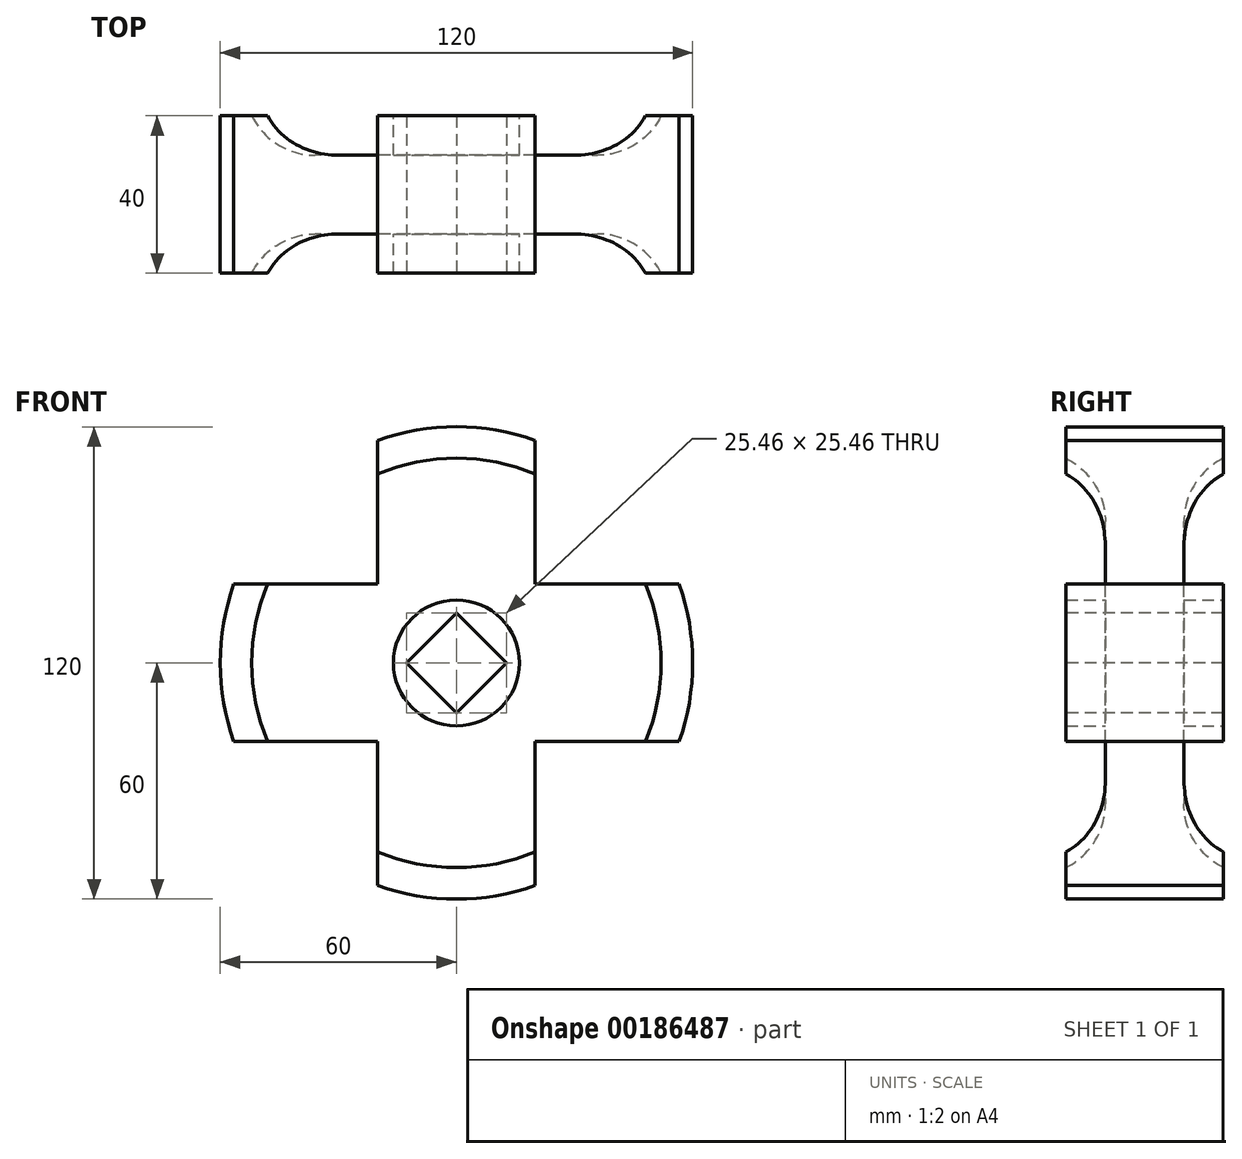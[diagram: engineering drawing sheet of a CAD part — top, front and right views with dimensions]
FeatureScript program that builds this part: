
annotation { "Feature Type Name" : "Feature", "Feature Type Description" : "" }
export const myFeature = defineFeature(function(context is Context, id is Id, definition is map)
    precondition{}
    {
        {
            var Q0;
            Q0=qCreatedBy(makeId("Top.planeOp"),FACE);
            var sketch = newSketch(context, id + "F0", { "sketchPlane" : qUnion([Q0])});
            skLineSegment(sketch, "E0", {"start": v(-60, 10) * mm, "end": v(-60, 20) * mm});
            skLineSegment(sketch, "E1", {"start": v(-60, 20) * mm, "end": v(-52, 20) * mm});
            skLineSegment(sketch, "E2", {"start": v(0, 20) * mm, "end": v(-16, 20) * mm});
            skLineSegment(sketch, "E3", {"start": v(-16, 20) * mm, "end": v(-16, 10) * mm});
            skPoint(sketch, "E4", {"position": v(-35.88, 10) * mm});
            skArc(sketch, "E5", {"start": v(-52, 20) * mm, "mid": v(-45.36, 12.7) * mm, "end": v(-35.88, 10) * mm});
            skArc(sketch, "E6.MirrorCS", {"start": v(-52, -20) * mm, "mid": v(-45.36, -12.7) * mm, "end": v(-35.88, -10) * mm});
            skLineSegment(sketch, "E7.MirrorCS", {"start": v(-60, -20) * mm, "end": v(-52, -20) * mm});
            skLineSegment(sketch, "E8.MirrorCS", {"start": v(-16, -20) * mm, "end": v(-16, -10) * mm});
            skLineSegment(sketch, "E9.MirrorCS", {"start": v(0, -20) * mm, "end": v(-16, -20) * mm});
            skLineSegment(sketch, "E10", {"start": v(-60, 10) * mm, "end": v(-60, -10) * mm});
            skLineSegment(sketch, "E11", {"start": v(-60, -10) * mm, "end": v(-60, -20) * mm});
            skLineSegment(sketch, "E12", {"start": v(0, 20) * mm, "end": v(0, -20) * mm});
            skLineSegment(sketch, "E13", {"start": v(0, 62.15) * mm, "end": v(0, -61.97) * mm, "construction": true});
            skPoint(sketch, "E14.start.orphan", {"position": v(0, 10) * mm});
            skPoint(sketch, "E15.orphan", {"position": v(-60, -10) * mm});
            skPoint(sketch, "E16.orphan", {"position": v(0, -10) * mm});
            skLineSegment(sketch, "E17", {"start": v(-16, 10) * mm, "end": v(-35.88, 10) * mm});
            skLineSegment(sketch, "E18", {"start": v(-16, -10) * mm, "end": v(-35.88, -10) * mm});
            skSolve(sketch);
        }
        {
            var Q0;
            Q0=makeQuery(id+"F0.imprint","IMPRINT",FACE,{"disambiguationData":[TD([[makeQuery(id+"F0.imprint","IMPRINT",EDGE,{"derivedFrom":sQuery(id+"F0.wireOp",EDGE,"E0")}),-1.0]])]});
            var Q1;
            Q1=sQuery(id+"F0.wireOp",EDGE,"E13");
            revolve(context, id + "F1", {"entities" : qUnion([Q0]), "axis" : qUnion([Q1]), "revolveType" : RevolveType.FULL});
        }
        {
            var Q0;
            Q0=makeQuery(id+"F1.opRevolve","SWEPT_FACE",FACE,{"disambiguationData":[OSD([sQuery(id+"F0.wireOp",EDGE,"E7.MirrorCS")])]});
            var sketch = newSketch(context, id + "F2", { "sketchPlane" : qUnion([Q0])});
            skLineSegment(sketch, "E19", {"start": v(0, 0) * mm, "end": v(0, -20) * mm});
            skLineSegment(sketch, "E20", {"start": v(0, 0) * mm, "end": v(0, 20) * mm});
            skLineSegment(sketch, "E21", {"start": v(0, 0) * mm, "end": v(-20, 0) * mm});
            skLineSegment(sketch, "E22", {"start": v(0, 0) * mm, "end": v(20, 0) * mm});
            skLineSegment(sketch, "E23", {"start": v(56.57, 20) * mm, "end": v(20, 20) * mm});
            skLineSegment(sketch, "E24.MirrorCS", {"start": v(56.57, -20) * mm, "end": v(20, -20) * mm});
            skLineSegment(sketch, "E25.MirrorCS", {"start": v(20, -56.57) * mm, "end": v(20, -20) * mm});
            skLineSegment(sketch, "E26.MirrorCS", {"start": v(-20, -56.57) * mm, "end": v(-20, -20) * mm});
            skLineSegment(sketch, "E27.MirrorCS", {"start": v(-56.57, -20) * mm, "end": v(-20, -20) * mm});
            skLineSegment(sketch, "E28.MirrorCS", {"start": v(-20, 56.57) * mm, "end": v(-20, 20) * mm});
            skLineSegment(sketch, "E29.MirrorCS", {"start": v(-56.57, 20) * mm, "end": v(-20, 20) * mm});
            skLineSegment(sketch, "E30", {"start": v(20, 20) * mm, "end": v(20, 56.57) * mm});
            skSolve(sketch);
        }
        {
            var Q0;
            {var subQ0=sQuery(id+"F2.wireOp",EDGE,"E23");var subQ1=sQuery(id+"F0.wireOp",EDGE,"E7.MirrorCS");var subQ2=makeQuery(id+"F1.opRevolve","SWEPT_EDGE",EDGE,{"disambiguationData":[OSD([subQ1,sQuery(id+"F0.wireOp",EDGE,"E11")])]});var subQ3=makeQuery(id+"F2.imprint","INTERSECT",VERTEX,{"derivedFrom":[subQ2,subQ0]});Q0=makeQuery(id+"F2.imprint","IMPRINT",FACE,{"disambiguationData":[TD([[makeQuery(id+"F2.imprint","IMPRINT",EDGE,{"disambiguationData":[TD([[subQ3,-1.0]])],"derivedFrom":subQ0}),-1.0]])]});}
            var Q1;
            {var subQ0=sQuery(id+"F2.wireOp",EDGE,"E30");var subQ1=sQuery(id+"F2.wireOp",EDGE,"E23");var subQ2=makeQuery(id+"F2.imprint","INTERSECT",VERTEX,{"derivedFrom":[subQ1,subQ0]});Q1=makeQuery(id+"F2.imprint","IMPRINT",FACE,{"disambiguationData":[TD([[makeQuery(id+"F2.imprint","IMPRINT",EDGE,{"disambiguationData":[TD([[subQ2,1.0]])],"derivedFrom":subQ1}),-1.0]])]});}
            var Q2;
            {var subQ0=sQuery(id+"F2.wireOp",EDGE,"E29.MirrorCS");var subQ1=sQuery(id+"F2.wireOp",EDGE,"E28.MirrorCS");var subQ2=makeQuery(id+"F2.imprint","INTERSECT",VERTEX,{"derivedFrom":[subQ1,subQ0]});Q2=makeQuery(id+"F2.imprint","IMPRINT",FACE,{"disambiguationData":[TD([[makeQuery(id+"F2.imprint","IMPRINT",EDGE,{"disambiguationData":[TD([[subQ2,1.0]])],"derivedFrom":subQ1}),-1.0]])]});}
            var Q3;
            {var subQ0=sQuery(id+"F2.wireOp",EDGE,"E28.MirrorCS");var subQ1=sQuery(id+"F0.wireOp",EDGE,"E7.MirrorCS");var subQ2=makeQuery(id+"F1.opRevolve","SWEPT_EDGE",EDGE,{"disambiguationData":[OSD([subQ1,sQuery(id+"F0.wireOp",EDGE,"E11")])]});var subQ3=makeQuery(id+"F2.imprint","INTERSECT",VERTEX,{"derivedFrom":[subQ2,subQ0]});Q3=makeQuery(id+"F2.imprint","IMPRINT",FACE,{"disambiguationData":[TD([[makeQuery(id+"F2.imprint","IMPRINT",EDGE,{"disambiguationData":[TD([[subQ3,-1.0]])],"derivedFrom":subQ0}),-1.0]])]});}
            var Q4;
            {var subQ0=sQuery(id+"F2.wireOp",EDGE,"E26.MirrorCS");var subQ1=sQuery(id+"F0.wireOp",EDGE,"E7.MirrorCS");var subQ2=makeQuery(id+"F1.opRevolve","SWEPT_EDGE",EDGE,{"disambiguationData":[OSD([subQ1,sQuery(id+"F0.wireOp",EDGE,"E11")])]});var subQ3=makeQuery(id+"F2.imprint","INTERSECT",VERTEX,{"derivedFrom":[subQ2,subQ0]});Q4=makeQuery(id+"F2.imprint","IMPRINT",FACE,{"disambiguationData":[TD([[makeQuery(id+"F2.imprint","IMPRINT",EDGE,{"disambiguationData":[TD([[subQ3,-1.0]])],"derivedFrom":subQ0}),1.0]])]});}
            var Q5;
            {var subQ0=sQuery(id+"F2.wireOp",EDGE,"E27.MirrorCS");var subQ1=sQuery(id+"F2.wireOp",EDGE,"E26.MirrorCS");var subQ2=makeQuery(id+"F2.imprint","INTERSECT",VERTEX,{"derivedFrom":[subQ1,subQ0]});Q5=makeQuery(id+"F2.imprint","IMPRINT",FACE,{"disambiguationData":[TD([[makeQuery(id+"F2.imprint","IMPRINT",EDGE,{"disambiguationData":[TD([[subQ2,1.0]])],"derivedFrom":subQ1}),1.0]])]});}
            var Q6;
            {var subQ0=sQuery(id+"F2.wireOp",EDGE,"E24.MirrorCS");var subQ1=sQuery(id+"F0.wireOp",EDGE,"E7.MirrorCS");var subQ2=makeQuery(id+"F1.opRevolve","SWEPT_EDGE",EDGE,{"disambiguationData":[OSD([subQ1,sQuery(id+"F0.wireOp",EDGE,"E11")])]});var subQ3=makeQuery(id+"F2.imprint","INTERSECT",VERTEX,{"derivedFrom":[subQ2,subQ0]});Q6=makeQuery(id+"F2.imprint","IMPRINT",FACE,{"disambiguationData":[TD([[makeQuery(id+"F2.imprint","IMPRINT",EDGE,{"disambiguationData":[TD([[subQ3,-1.0]])],"derivedFrom":subQ0}),1.0]])]});}
            var Q7;
            {var subQ0=sQuery(id+"F2.wireOp",EDGE,"E25.MirrorCS");var subQ1=sQuery(id+"F2.wireOp",EDGE,"E24.MirrorCS");var subQ2=makeQuery(id+"F2.imprint","INTERSECT",VERTEX,{"derivedFrom":[subQ1,subQ0]});Q7=makeQuery(id+"F2.imprint","IMPRINT",FACE,{"disambiguationData":[TD([[makeQuery(id+"F2.imprint","IMPRINT",EDGE,{"disambiguationData":[TD([[subQ2,1.0]])],"derivedFrom":subQ1}),1.0]])]});}
            extrude(context, id + "F3", {"entities" : qUnion([Q0, Q1, Q2, Q3, Q4, Q5, Q6, Q7]), "operationType" : NewBodyOperationType.REMOVE, "endBound" : BoundingType.THROUGH_ALL, "oppositeDirection" : true, "depth" : 25 * mm});
        }
        {
            var Q0;
            Q0=makeQuery(id+"F1.opRevolve","SWEPT_FACE",FACE,{"disambiguationData":[OSD([sQuery(id+"F0.wireOp",EDGE,"E9.MirrorCS")])]});
            var sketch = newSketch(context, id + "F4", { "sketchPlane" : qUnion([Q0])});
            skLineSegment(sketch, "E31", {"start": v(12.73, 0) * mm, "end": v(0, 12.73) * mm});
            skLineSegment(sketch, "E32", {"start": v(-12.73, 0) * mm, "end": v(0, 12.73) * mm});
            skLineSegment(sketch, "E33", {"start": v(0, -12.73) * mm, "end": v(-12.73, 0) * mm});
            skLineSegment(sketch, "E34", {"start": v(0, -12.73) * mm, "end": v(12.73, 0) * mm});
            skSolve(sketch);
        }
        {
            var Q0;
            Q0=makeQuery(id+"F4.imprint","IMPRINT",FACE,{"disambiguationData":[TD([[makeQuery(id+"F4.imprint","IMPRINT",EDGE,{"derivedFrom":sQuery(id+"F4.wireOp",EDGE,"E31")}),1.0]])]});
            extrude(context, id + "F5", {"entities" : qUnion([Q0]), "operationType" : NewBodyOperationType.REMOVE, "endBound" : BoundingType.THROUGH_ALL, "oppositeDirection" : true, "depth" : 25 * mm});
        }
    });
